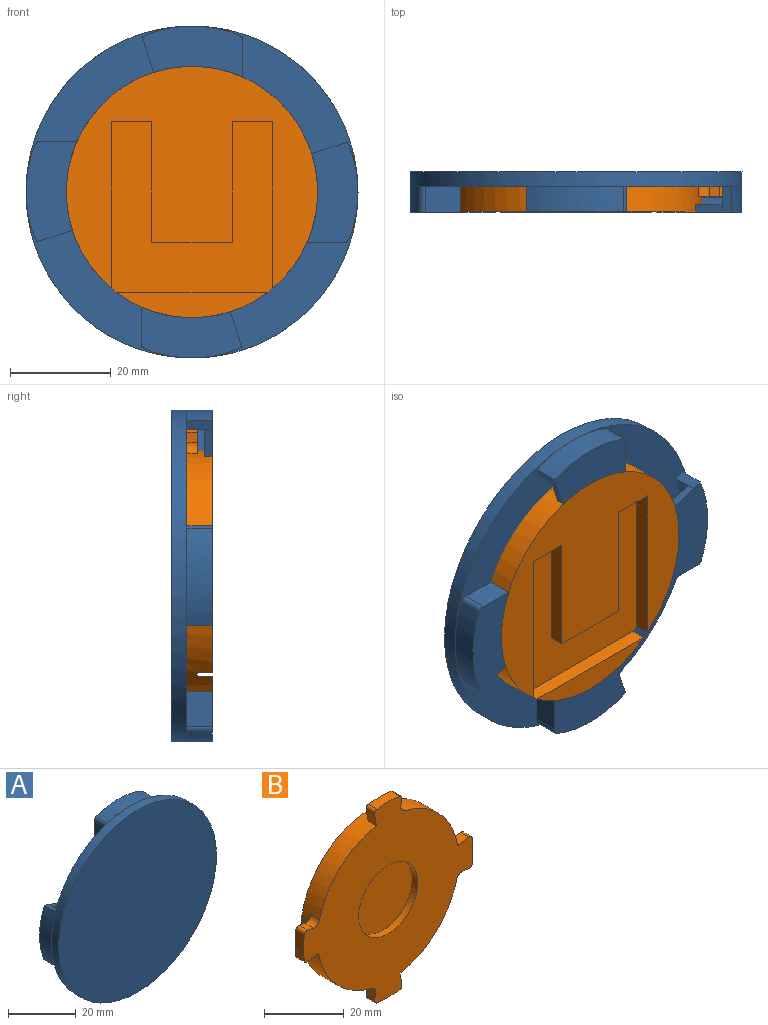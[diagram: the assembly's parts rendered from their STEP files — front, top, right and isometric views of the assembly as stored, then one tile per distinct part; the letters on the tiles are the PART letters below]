
ASSEMBLY  parts=2 mates=1
PART A: 49 faces, bbox 66x8x66 mm
  f0: plane 4.47x3.5mm, normal (0.17,0,-0.99), area 15.9mm2, adj f1,f12,f35,f46
  f1: cylinder r=1mm len=3.5mm, axis (0,-1,0), area 5.4mm2, adj f0,f2,f12,f46
  f2: cylinder r=25mm len=13.4mm, axis (0,-1,0), area 47.7mm2, adj f1,f12,f36,f46
  f3: plane 4.47x3.5mm, normal (-0.99,0,-0.17), area 15.9mm2, adj f4,f12,f29,f44
  f4: cylinder r=1mm len=3.5mm, axis (0,-1,0), area 5.4mm2, adj f3,f5,f12,f44
  f5: cylinder r=25mm len=13.4mm, axis (0,-1,0), area 47.7mm2, adj f4,f12,f30,f44
  f6: plane 4.47x3.5mm, normal (-0.17,0,0.99), area 15.9mm2, adj f7,f12,f23,f42
  f7: cylinder r=1mm len=3.5mm, axis (0,-1,0), area 5.4mm2, adj f6,f8,f12,f42
  f8: cylinder r=25mm len=13.4mm, axis (0,-1,0), area 47.7mm2, adj f7,f12,f24,f42
  f9: plane 4.47x3.5mm, normal (0.99,0,0.17), area 15.9mm2, adj f10,f12,f19,f40
  f10: cylinder r=1mm len=3.5mm, axis (0,-1,0), area 5.4mm2, adj f9,f11,f12,f40
  f11: cylinder r=25mm len=13.4mm, axis (0,-1,0), area 47.7mm2, adj f10,f12,f15,f40
  f12: plane 66.04x66.04mm, normal (0,1,0), area 2775.2mm2, adj f0,f1,f2,f3,f4,f5,f6,f7
  f13: cylinder r=33.02mm len=66.04mm, axis (0,1,0), area 622.4mm2, adj f12,f14
  f14: plane 66.04x66.04mm, normal (0,-1,0), area 3425.1mm2, adj f13
  f15: plane 5x1.89mm, normal (0.94,0,-0.33), area 10mm2, adj f11,f12,f16,f20,f39
  f16: cylinder r=25mm len=19.35mm, axis (0,-1,0), area 99.4mm2, adj f12,f15,f17,f20
  f17: cylinder r=1mm len=5mm, axis (0,-1,0), area 7.5mm2, adj f12,f16,f18,f20
  f18: plane 7.04x5mm, normal (-1,0,0), area 35.2mm2, adj f12,f17,f19,f20
  f19: cylinder r=25mm len=17.59mm, axis (0,-1,0), area 48.3mm2, adj f9,f12,f18,f20,f39,f40
  f20: plane 19.98x10.1mm, normal (0,1,0), area 150.3mm2, adj f15,f16,f17,f18,f19,f39
  f21: cylinder r=1mm len=5mm, axis (0,-1,0), area 7.5mm2, adj f12,f22,f25,f26
  f22: plane 7.04x5mm, normal (0,0,-1), area 35.2mm2, adj f12,f21,f23,f26
  f23: cylinder r=25mm len=17.59mm, axis (0,-1,0), area 48.3mm2, adj f6,f12,f22,f26,f41,f42
  f24: plane 5x1.89mm, normal (0.33,0,0.94), area 10mm2, adj f8,f12,f25,f26,f41
  f25: cylinder r=25mm len=19.35mm, axis (0,-1,0), area 99.4mm2, adj f12,f21,f24,f26
  f26: plane 19.98x10.1mm, normal (0,1,0), area 150.3mm2, adj f21,f22,f23,f24,f25,f41
  f27: cylinder r=1mm len=5mm, axis (0,-1,0), area 7.5mm2, adj f12,f28,f31,f32
  f28: plane 7.04x5mm, normal (1,0,0), area 35.2mm2, adj f12,f27,f29,f32
  f29: cylinder r=25mm len=17.59mm, axis (0,-1,0), area 48.3mm2, adj f3,f12,f28,f32,f43,f44
  f30: plane 5x1.89mm, normal (-0.94,0,0.33), area 10mm2, adj f5,f12,f31,f32,f43
  f31: cylinder r=25mm len=19.35mm, axis (0,-1,0), area 99.4mm2, adj f12,f27,f30,f32
  f32: plane 19.98x10.1mm, normal (0,1,0), area 150.3mm2, adj f27,f28,f29,f30,f31,f43
  f33: cylinder r=1mm len=5mm, axis (0,-1,0), area 7.5mm2, adj f12,f34,f37,f38
  f34: plane 7.04x5mm, normal (0,0,1), area 35.2mm2, adj f12,f33,f35,f38
  f35: cylinder r=25mm len=17.59mm, axis (0,-1,0), area 48.3mm2, adj f0,f12,f34,f38,f45,f46
  f36: plane 5x1.89mm, normal (-0.33,0,-0.94), area 10mm2, adj f2,f12,f37,f38,f45
  f37: cylinder r=25mm len=19.35mm, axis (0,-1,0), area 99.4mm2, adj f12,f33,f36,f38
  f38: plane 19.98x10.1mm, normal (0,1,0), area 150.3mm2, adj f33,f34,f35,f36,f37,f45
  f39: plane 5.23x1.67mm, normal (0.95,0,-0.3), area 8.2mm2, adj f15,f19,f20,f40
  f40: plane 14.21x6.87mm, normal (0,-1,0), area 74.4mm2, adj f9,f10,f11,f19,f39
  f41: plane 5.23x1.67mm, normal (0.3,0,0.95), area 8.2mm2, adj f23,f24,f26,f42
  f42: plane 14.21x6.87mm, normal (0,-1,0), area 74.4mm2, adj f6,f7,f8,f23,f41
  f43: plane 5.23x1.67mm, normal (-0.95,0,0.3), area 8.2mm2, adj f29,f30,f32,f44
  f44: plane 14.21x6.87mm, normal (0,-1,0), area 74.4mm2, adj f3,f4,f5,f29,f43
  f45: plane 5.23x1.67mm, normal (-0.3,0,-0.95), area 8.2mm2, adj f35,f36,f38,f46
  f46: plane 14.21x6.87mm, normal (0,-1,0), area 74.4mm2, adj f0,f1,f2,f35,f45
  f47: cylinder r=10.5mm len=21mm, axis (0,1,0), area 131.9mm2, adj f12,f48
  f48: plane 21x21mm, normal (0,1,0), area 346.4mm2, adj f47
PART B: 43 faces, bbox 60x6x60 mm
  f0: cylinder r=25mm len=50mm, axis (0,1,0), area 812.1mm2, adj f1,f2,f3,f4,f5,f11,f12,f13
  f1: plane 30x5mm, normal (0,1,0), area 102.2mm2, adj f0,f4
  f2: plane 50x44.21mm, normal (0,1,0), area 1158.1mm2, adj f0,f5,f6,f7,f8,f9,f10,f11
  f3: plane 60x60mm, normal (0,-1,0), area 1802.6mm2, adj f0,f13,f14,f15,f16,f17,f18,f20
  f4: plane 30x3mm, normal (0,0,1), area 90mm2, adj f0,f1,f12
  f5: plane 33.21x3mm, normal (1,0,0), area 99.6mm2, adj f0,f2,f6,f12
  f6: plane 8x3mm, normal (0,0,-1), area 24mm2, adj f2,f5,f7,f12
  f7: plane 24x3mm, normal (-1,0,0), area 72mm2, adj f2,f6,f8,f12
  f8: plane 16x3mm, normal (0,0,-1), area 48mm2, adj f2,f7,f9,f12
  f9: plane 24x3mm, normal (1,0,0), area 72mm2, adj f2,f8,f10,f12
  f10: plane 8x3mm, normal (0,0,-1), area 24mm2, adj f2,f9,f11,f12
  f11: plane 33.21x3mm, normal (-1,0,0), area 99.6mm2, adj f0,f2,f10,f12
  f12: plane 34x32mm, normal (0,1,0), area 703.2mm2, adj f0,f4,f5,f6,f7,f8,f9,f10
  f13: cylinder r=2mm len=3mm, axis (0,-1,0), area 9mm2, adj f0,f3,f14,f19
  f14: plane 3x2.03mm, normal (0.17,0,0.99), area 6.2mm2, adj f3,f13,f15,f19
  f15: cylinder r=1mm len=3mm, axis (0,-1,0), area 4.8mm2, adj f3,f14,f16,f19
  f16: cylinder r=30mm len=7.95mm, axis (0,-1,0), area 23.9mm2, adj f3,f15,f17,f19
  f17: cylinder r=1mm len=3mm, axis (0,-1,0), area 4.8mm2, adj f3,f16,f18,f19
  f18: plane 3.93x3mm, normal (0.17,0,-0.99), area 11.9mm2, adj f0,f3,f17,f19
  f19: plane 10.83x5.73mm, normal (0,1,0), area 46.4mm2, adj f0,f13,f14,f15,f16,f17,f18
  f20: cylinder r=2mm len=3mm, axis (0,-1,0), area 9mm2, adj f0,f3,f21,f26
  f21: plane 3x2.03mm, normal (0.99,0,-0.17), area 6.2mm2, adj f3,f20,f22,f26
  f22: cylinder r=1mm len=3mm, axis (0,-1,0), area 4.8mm2, adj f3,f21,f23,f26
  f23: cylinder r=30mm len=7.95mm, axis (0,-1,0), area 23.9mm2, adj f3,f22,f24,f26
  f24: cylinder r=1mm len=3mm, axis (0,-1,0), area 4.8mm2, adj f3,f23,f25,f26
  f25: plane 3.93x3mm, normal (-0.99,0,-0.17), area 11.9mm2, adj f0,f3,f24,f26
  f26: plane 10.83x5.73mm, normal (0,1,0), area 46.4mm2, adj f0,f20,f21,f22,f23,f24,f25
  f27: cylinder r=2mm len=3mm, axis (0,-1,0), area 9mm2, adj f0,f3,f28,f33
  f28: plane 3x2.03mm, normal (-0.99,0,0.17), area 6.2mm2, adj f3,f27,f29,f33
  f29: cylinder r=1mm len=3mm, axis (0,-1,0), area 4.8mm2, adj f3,f28,f30,f33
  f30: cylinder r=30mm len=7.95mm, axis (0,-1,0), area 23.9mm2, adj f3,f29,f31,f33
  f31: cylinder r=1mm len=3mm, axis (0,-1,0), area 4.8mm2, adj f3,f30,f32,f33
  f32: plane 3.93x3mm, normal (0.99,0,0.17), area 11.9mm2, adj f0,f3,f31,f33
  f33: plane 10.83x5.73mm, normal (0,1,0), area 46.4mm2, adj f0,f27,f28,f29,f30,f31,f32
  f34: cylinder r=2mm len=3mm, axis (0,-1,0), area 9mm2, adj f0,f3,f35,f40
  f35: plane 3x2.03mm, normal (-0.17,0,-0.99), area 6.2mm2, adj f3,f34,f36,f40
  f36: cylinder r=1mm len=3mm, axis (0,-1,0), area 4.8mm2, adj f3,f35,f37,f40
  f37: cylinder r=30mm len=7.95mm, axis (0,-1,0), area 23.9mm2, adj f3,f36,f38,f40
  f38: cylinder r=1mm len=3mm, axis (0,-1,0), area 4.8mm2, adj f3,f37,f39,f40
  f39: plane 3.93x3mm, normal (-0.17,0,0.99), area 11.9mm2, adj f0,f3,f38,f40
  f40: plane 10.83x5.73mm, normal (0,1,0), area 46.4mm2, adj f0,f34,f35,f36,f37,f38,f39
  f41: cylinder r=10.5mm len=21mm, axis (0,-1,0), area 131.9mm2, adj f3,f42
  f42: plane 21x21mm, normal (0,-1,0), area 346.4mm2, adj f41
PLACE A rot(axis=(1,0,0),180deg) t=(0,-9,0)mm
PLACE B rot(axis=(0,0,-1),180deg) t=(0,-8,0)mm
MATE cylindrical B.f41 <-> A.f19  axis (0,1,0) through (0,-3,0)mm
